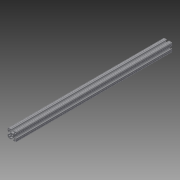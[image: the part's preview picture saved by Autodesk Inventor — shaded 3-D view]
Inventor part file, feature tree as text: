
AUTODESK INVENTOR PART (.ipt)
format: ipt  version: 2013 (Build 170138000, 138)  size: 288,256 bytes
history: native  units: in
note: dims shown in document units (in); Inventor stores cm internally (conversion verified against a paired STEP export)
features: extrude x1, sketch x1
ambient origin geometry x8: Origin, YZ Plane, XZ Plane, XY Plane, X Axis, Y Axis, Z Axis, Center Point
bodies: Solid1 (feature_tree)
feature tree (2):
  extrude  "Extrusion1"  [1 undecoded]
  sketch  "Sketch1"  dims[d0=27.0in d1=0.0in]
note: 1 required parameter value undecoded (feature->parameter linkage not recoverable at this tier; creation-order binding heuristic only, values carry confidence <= 0.55)
